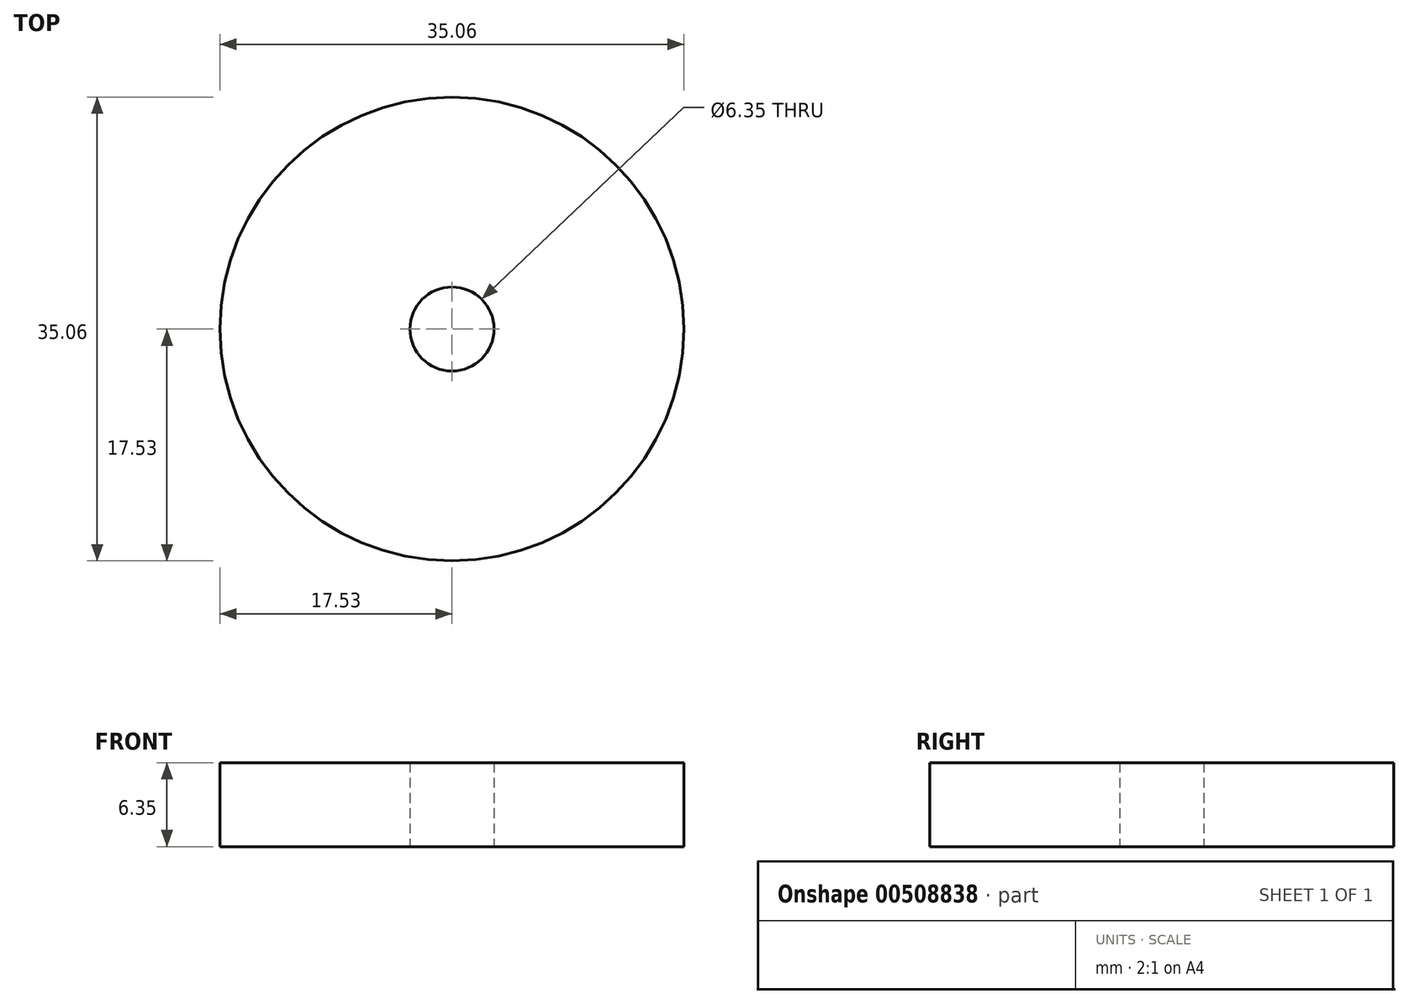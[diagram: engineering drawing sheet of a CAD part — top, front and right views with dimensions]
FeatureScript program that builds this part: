
annotation { "Feature Type Name" : "Feature", "Feature Type Description" : "" }
export const myFeature = defineFeature(function(context is Context, id is Id, definition is map)
    precondition{}
    {
        {
            var Q0;
            Q0=qCreatedBy(makeId("Top.planeOp"),FACE);
            var sketch = newSketch(context, id + "F0", { "sketchPlane" : qUnion([Q0])});
            skCircle(sketch, "E0", {"center": v(0, 0) * mm, "radius": 17.53 * mm});
            skCircle(sketch, "E1", {"center": v(0, 0) * mm, "radius": 3.18 * mm});
            skSolve(sketch);
        }
        {
            var Q0;
            Q0=makeQuery(id+"F0.imprint","IMPRINT",FACE,{"disambiguationData":[TD([[makeQuery(id+"F0.imprint","IMPRINT",EDGE,{"derivedFrom":sQuery(id+"F0.wireOp",EDGE,"E0")}),1.0]])]});
            extrude(context, id + "F1", {"entities" : qUnion([Q0]), "depth" : 6.35 * mm});
        }
    });
